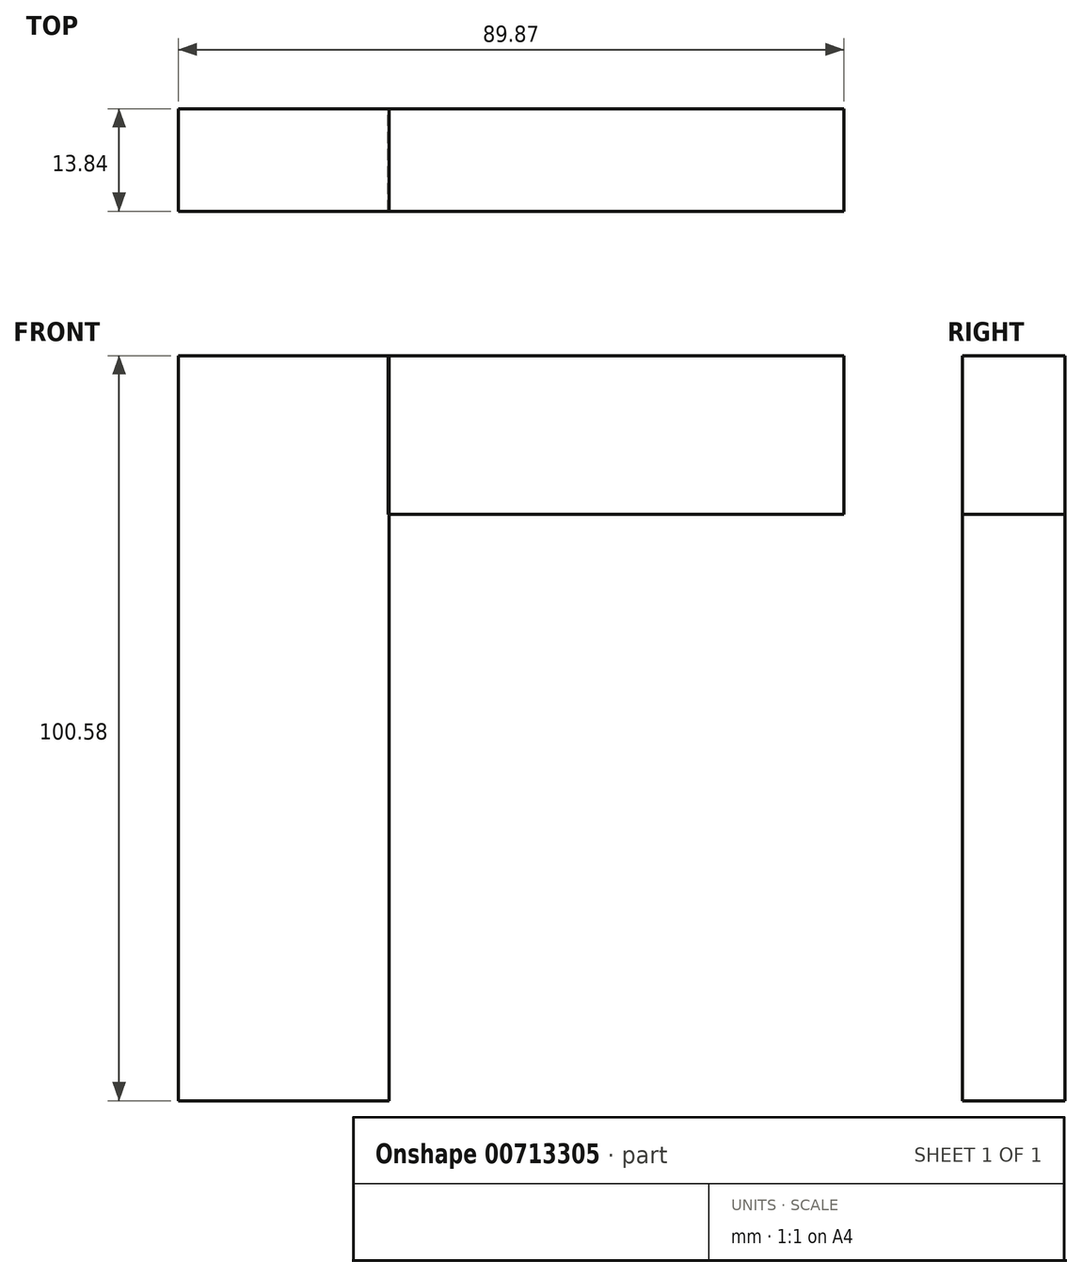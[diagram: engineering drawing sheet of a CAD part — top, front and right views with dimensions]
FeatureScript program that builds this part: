
annotation { "Feature Type Name" : "Feature", "Feature Type Description" : "" }
export const myFeature = defineFeature(function(context is Context, id is Id, definition is map)
    precondition{}
    {
        {
            var Q0;
            Q0=qCreatedBy(makeId("Front.planeOp"),FACE);
            var sketch = newSketch(context, id + "F0", { "sketchPlane" : qUnion([Q0])});
            skLineSegment(sketch, "E0.bottom", {"start": v(-14.22, -50.29) * mm, "end": v(14.22, -50.29) * mm});
            skLineSegment(sketch, "E0.top", {"start": v(-14.22, 50.29) * mm, "end": v(14.22, 50.29) * mm});
            skLineSegment(sketch, "E0.left", {"start": v(-14.22, -50.29) * mm, "end": v(-14.22, 50.29) * mm});
            skLineSegment(sketch, "E0.right", {"start": v(14.22, -50.29) * mm, "end": v(14.22, 50.29) * mm});
            skPoint(sketch, "E0.middle", {"position": v(0, 0) * mm});
            skLineSegment(sketch, "E1.bottom", {"start": v(14.22, -50.29) * mm, "end": v(-14.59, -50.29) * mm, "construction": true});
            skLineSegment(sketch, "E1.top", {"start": v(14.22, -67.54) * mm, "end": v(-14.59, -67.54) * mm, "construction": true});
            skLineSegment(sketch, "E1.left", {"start": v(14.22, -50.29) * mm, "end": v(14.22, -67.54) * mm, "construction": true});
            skLineSegment(sketch, "E1.right", {"start": v(-14.59, -50.29) * mm, "end": v(-14.59, -67.54) * mm, "construction": true});
            skLineSegment(sketch, "E2.bottom", {"start": v(14.22, -58.91) * mm, "end": v(14.22, -58.91) * mm});
            skLineSegment(sketch, "E2.top", {"start": v(14.22, -58.91) * mm, "end": v(14.22, -58.91) * mm});
            skLineSegment(sketch, "E2.left", {"start": v(14.22, -58.91) * mm, "end": v(14.22, -58.91) * mm});
            skLineSegment(sketch, "E2.right", {"start": v(14.22, -58.91) * mm, "end": v(14.22, -58.91) * mm});
            skSolve(sketch);
        }
        {
            var Q0;
            Q0=qCreatedBy(makeId("Front.planeOp"),FACE);
            var sketch = newSketch(context, id + "F1", { "sketchPlane" : qUnion([Q0])});
            skLineSegment(sketch, "E3.bottom", {"start": v(14.1, 50.28) * mm, "end": v(75.65, 50.28) * mm});
            skLineSegment(sketch, "E3.top", {"start": v(14.1, 28.9) * mm, "end": v(75.65, 28.9) * mm});
            skLineSegment(sketch, "E3.left", {"start": v(14.1, 50.28) * mm, "end": v(14.1, 28.9) * mm});
            skLineSegment(sketch, "E3.right", {"start": v(75.65, 50.28) * mm, "end": v(75.65, 28.9) * mm});
            skSolve(sketch);
        }
        {
            var Q0;
            Q0=makeQuery(id+"F1.imprint","IMPRINT",FACE,{"disambiguationData":[TD([[makeQuery(id+"F1.imprint","IMPRINT",EDGE,{"derivedFrom":sQuery(id+"F1.wireOp",EDGE,"E3.bottom")}),-1.0]])]});
            var Q1;
            Q1=makeQuery(id+"F0.imprint","IMPRINT",FACE,{"disambiguationData":[TD([[makeQuery(id+"F0.imprint","IMPRINT",EDGE,{"derivedFrom":sQuery(id+"F0.wireOp",EDGE,"E0.bottom")}),1.0]])]});
            extrude(context, id + "F2", {"entities" : qUnion([Q0, Q1]), "depth" : 13.84 * mm, "offsetDistance" : 25.4 * mm});
        }
    });
